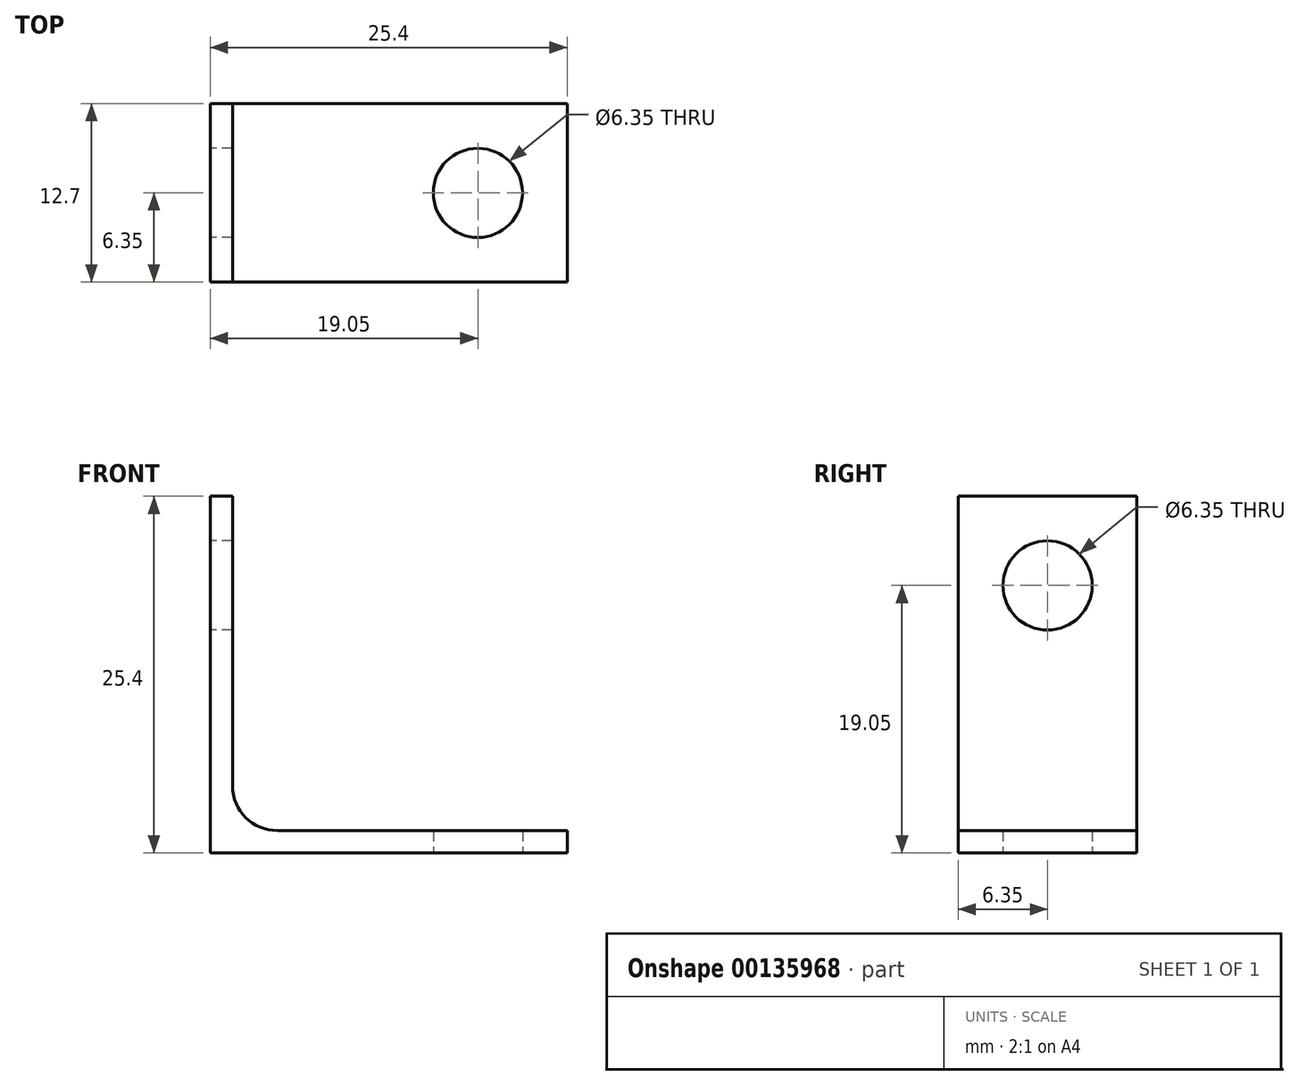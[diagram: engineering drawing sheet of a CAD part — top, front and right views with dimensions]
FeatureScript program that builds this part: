
annotation { "Feature Type Name" : "Feature", "Feature Type Description" : "" }
export const myFeature = defineFeature(function(context is Context, id is Id, definition is map)
    precondition{}
    {
        {
            var Q0;
            Q0=qCreatedBy(makeId("Right.planeOp"),FACE);
            var sketch = newSketch(context, id + "F0", { "sketchPlane" : qUnion([Q0])});
            skLineSegment(sketch, "E0", {"start": v(0, 0) * mm, "end": v(-12.7, 0) * mm});
            skLineSegment(sketch, "E1", {"start": v(-12.7, 0) * mm, "end": v(-12.7, 25.4) * mm});
            skLineSegment(sketch, "E2", {"start": v(-12.7, 25.4) * mm, "end": v(0, 25.4) * mm});
            skLineSegment(sketch, "E3", {"start": v(0, 25.4) * mm, "end": v(0, 0) * mm});
            skCircle(sketch, "E4", {"center": v(-6.35, 19.05) * mm, "radius": 3.18 * mm});
            skSolve(sketch);
        }
        {
            var Q0;
            Q0=makeQuery(id+"F0.imprint","IMPRINT",FACE,{"disambiguationData":[TD([[makeQuery(id+"F0.imprint","IMPRINT",EDGE,{"derivedFrom":sQuery(id+"F0.wireOp",EDGE,"E0")}),-1.0]])]});
            extrude(context, id + "F1", {"entities" : qUnion([Q0]), "depth" : 1.6 * mm});
        }
        {
            var Q0;
            Q0=qCreatedBy(makeId("Top.planeOp"),FACE);
            var sketch = newSketch(context, id + "F2", { "sketchPlane" : qUnion([Q0])});
            skLineSegment(sketch, "E5", {"start": v(0, 0) * mm, "end": v(25.4, 0) * mm});
            skLineSegment(sketch, "E6", {"start": v(25.4, 0) * mm, "end": v(25.4, -12.7) * mm});
            skLineSegment(sketch, "E7", {"start": v(25.4, -12.7) * mm, "end": v(0, -12.7) * mm});
            skLineSegment(sketch, "E8", {"start": v(0, -12.7) * mm, "end": v(0, 0) * mm});
            skCircle(sketch, "E9", {"center": v(19.05, -6.35) * mm, "radius": 3.18 * mm});
            skSolve(sketch);
        }
        {
            var Q0;
            Q0=makeQuery(id+"F2.imprint","IMPRINT",FACE,{"disambiguationData":[TD([[makeQuery(id+"F2.imprint","IMPRINT",EDGE,{"derivedFrom":sQuery(id+"F2.wireOp",EDGE,"E5")}),-1.0]])]});
            extrude(context, id + "F3", {"entities" : qUnion([Q0]), "operationType" : NewBodyOperationType.ADD, "depth" : 1.6 * mm});
        }
        {
            var Q0;
            Q0=makeQuery(id+"F3.boolean.opBoolean","INTERSECT",EDGE,{"derivedFrom":[makeQuery(id+"F1.opExtrude","CAP_FACE",FACE,{"disambiguationData":[OSD([sQuery(id+"F0.wireOp",EDGE,"E0"),sQuery(id+"F0.wireOp",EDGE,"E1"),sQuery(id+"F0.wireOp",EDGE,"E2"),sQuery(id+"F0.wireOp",EDGE,"E3"),sQuery(id+"F0.wireOp",EDGE,"E4")])],"isStart":false}),makeQuery(id+"F3.opExtrude","CAP_FACE",FACE,{"disambiguationData":[OSD([sQuery(id+"F2.wireOp",EDGE,"E5"),sQuery(id+"F2.wireOp",EDGE,"E6"),sQuery(id+"F2.wireOp",EDGE,"E7"),sQuery(id+"F2.wireOp",EDGE,"E8"),sQuery(id+"F2.wireOp",EDGE,"E9")])],"isStart":false})]});
            fillet(context, id + "F4", {"entities" : qUnion([Q0]), "radius" : 3.17 * mm, "tangentPropagation" : true, "allowEdgeOverflow" : false});
        }
    });
